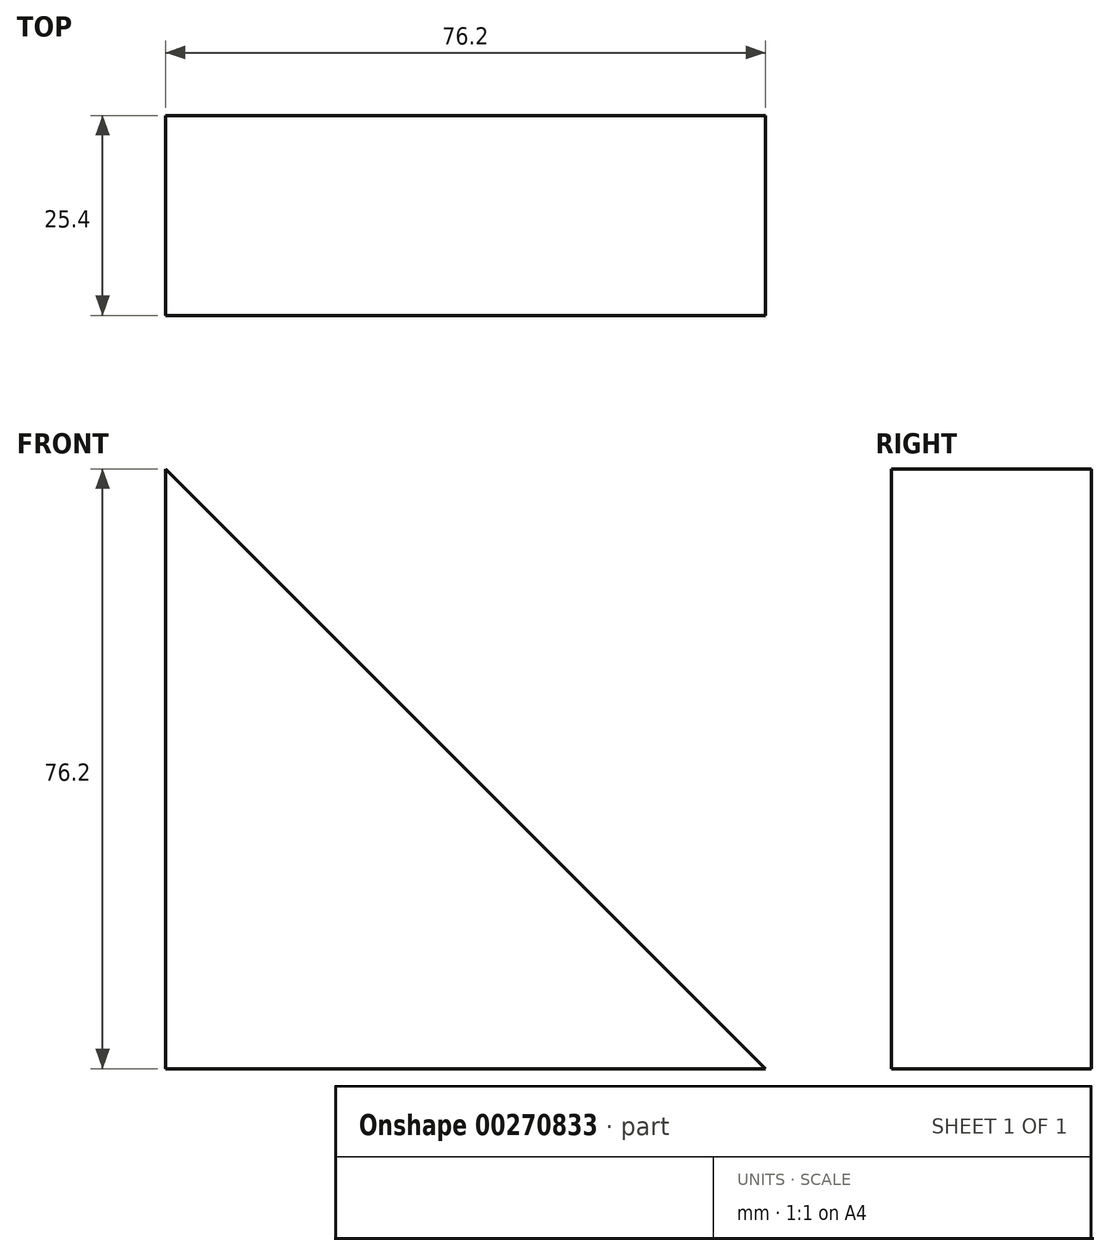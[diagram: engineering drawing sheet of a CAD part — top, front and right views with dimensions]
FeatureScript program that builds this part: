
annotation { "Feature Type Name" : "Feature", "Feature Type Description" : "" }
export const myFeature = defineFeature(function(context is Context, id is Id, definition is map)
    precondition{}
    {
        {
            var Q0;
            Q0=qCreatedBy(makeId("Front.planeOp"),FACE);
            var sketch = newSketch(context, id + "F0", { "sketchPlane" : qUnion([Q0])});
            skLineSegment(sketch, "E0", {"start": v(-76.2, 0) * mm, "end": v(-76.2, 76.2) * mm});
            skLineSegment(sketch, "E1", {"start": v(-76.2, 0) * mm, "end": v(0, 0) * mm});
            skLineSegment(sketch, "E2", {"start": v(0, 0) * mm, "end": v(-76.2, 76.2) * mm});
            skSolve(sketch);
        }
        {
            var Q0;
            Q0 = qSketchRegion(id + "F0", true);
            extrude(context, id + "F1", {"entities" : qUnion([Q0]), "depth" : 25.4 * mm});
        }
    });
